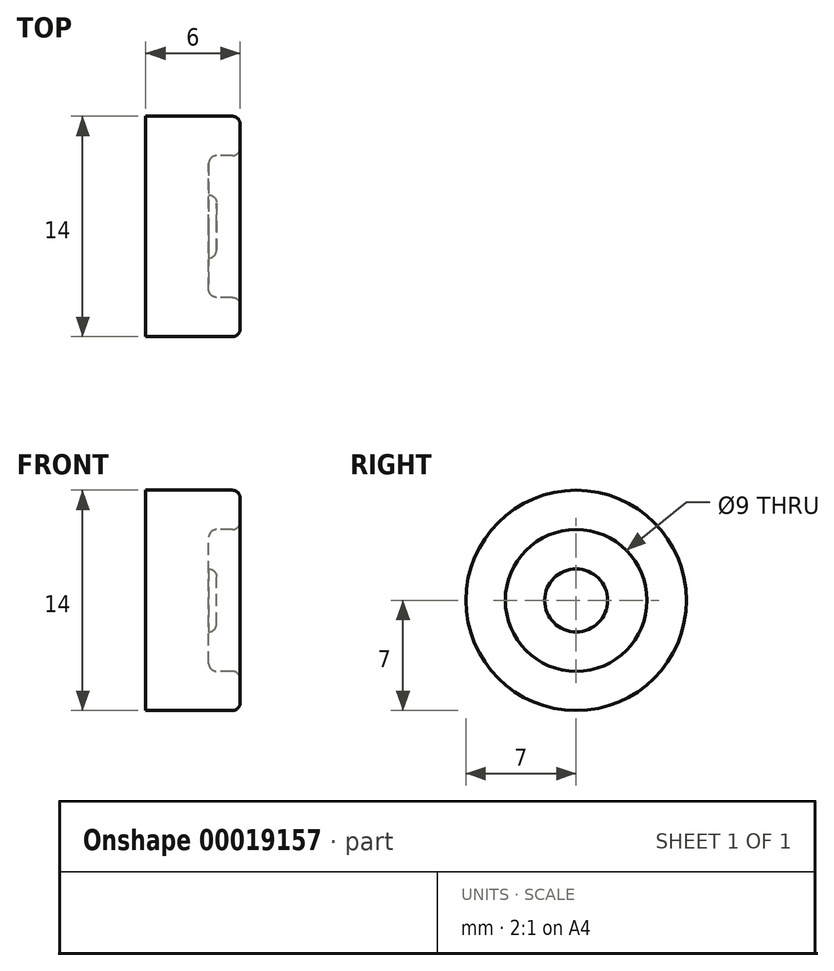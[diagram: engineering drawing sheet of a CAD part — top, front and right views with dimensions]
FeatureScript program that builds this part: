
annotation { "Feature Type Name" : "Feature", "Feature Type Description" : "" }
export const myFeature = defineFeature(function(context is Context, id is Id, definition is map)
    precondition{}
    {
        {
            var Q0;
            Q0=qCreatedBy(makeId("Top.planeOp"),FACE);
            var sketch = newSketch(context, id + "F0", { "sketchPlane" : qUnion([Q0])});
            skLineSegment(sketch, "E0", {"start": v(0, 0) * mm, "end": v(10.7, 0) * mm});
            skLineSegment(sketch, "E1.bottom", {"start": v(0, 7) * mm, "end": v(6, 7) * mm});
            skLineSegment(sketch, "E1.top", {"start": v(0, 4.5) * mm, "end": v(6, 4.5) * mm});
            skLineSegment(sketch, "E1.left", {"start": v(0, 7) * mm, "end": v(0, 4.5) * mm});
            skLineSegment(sketch, "E1.right", {"start": v(6, 7) * mm, "end": v(6, 4.5) * mm});
            skLineSegment(sketch, "E2.bottom", {"start": v(0, 4.5) * mm, "end": v(4, 4.5) * mm});
            skLineSegment(sketch, "E2.top", {"start": v(0, 0) * mm, "end": v(4, 0) * mm});
            skLineSegment(sketch, "E2.left", {"start": v(0, 4.5) * mm, "end": v(0, 0) * mm});
            skLineSegment(sketch, "E2.right", {"start": v(4, 4.5) * mm, "end": v(4, 0) * mm});
            skLineSegment(sketch, "E3.bottom", {"start": v(4, 2) * mm, "end": v(4.5, 2) * mm});
            skLineSegment(sketch, "E3.top", {"start": v(4, 0) * mm, "end": v(4.5, 0) * mm});
            skLineSegment(sketch, "E3.left", {"start": v(4, 2) * mm, "end": v(4, 0) * mm});
            skLineSegment(sketch, "E3.right", {"start": v(4.5, 2) * mm, "end": v(4.5, 0) * mm});
            skSolve(sketch);
        }
        {
            var Q0;
            Q0 = qSketchRegion(id + "F0", true);
            var Q1;
            Q1=sQuery(id+"F0.wireOp",EDGE,"E0");
            revolve(context, id + "F1", {"entities" : qUnion([Q0]), "axis" : qUnion([Q1]), "revolveType" : RevolveType.FULL});
        }
        {
            var Q0;
            Q0=makeQuery(id+"F1.opRevolve","SWEPT_EDGE",EDGE,{"disambiguationData":[OSD([sQuery(id+"F0.wireOp",EDGE,"E1.bottom"),sQuery(id+"F0.wireOp",EDGE,"E1.right")])]});
            var Q1;
            Q1=makeQuery(id+"F1.opRevolve","SWEPT_EDGE",EDGE,{"disambiguationData":[OSD([sQuery(id+"F0.wireOp",EDGE,"E1.top"),sQuery(id+"F0.wireOp",EDGE,"E1.right")])]});
            var Q2;
            Q2=makeQuery(id+"F1.opRevolve","SWEPT_EDGE",EDGE,{"disambiguationData":[OSD([sQuery(id+"F0.wireOp",EDGE,"E3.bottom"),sQuery(id+"F0.wireOp",EDGE,"E3.right")])]});
            var Q3;
            Q3=makeQuery(id+"F1.opRevolve","SWEPT_EDGE",EDGE,{"disambiguationData":[OSD([sQuery(id+"F0.wireOp",EDGE,"E1.top"),sQuery(id+"F0.wireOp",EDGE,"E2.bottom"),sQuery(id+"F0.wireOp",EDGE,"E2.right")])]});
            fillet(context, id + "F2", {"entities" : qUnion([Q0, Q1, Q2, Q3]), "radius" : .5 * mm, "tangentPropagation" : true, "allowEdgeOverflow" : false});
        }
    });
